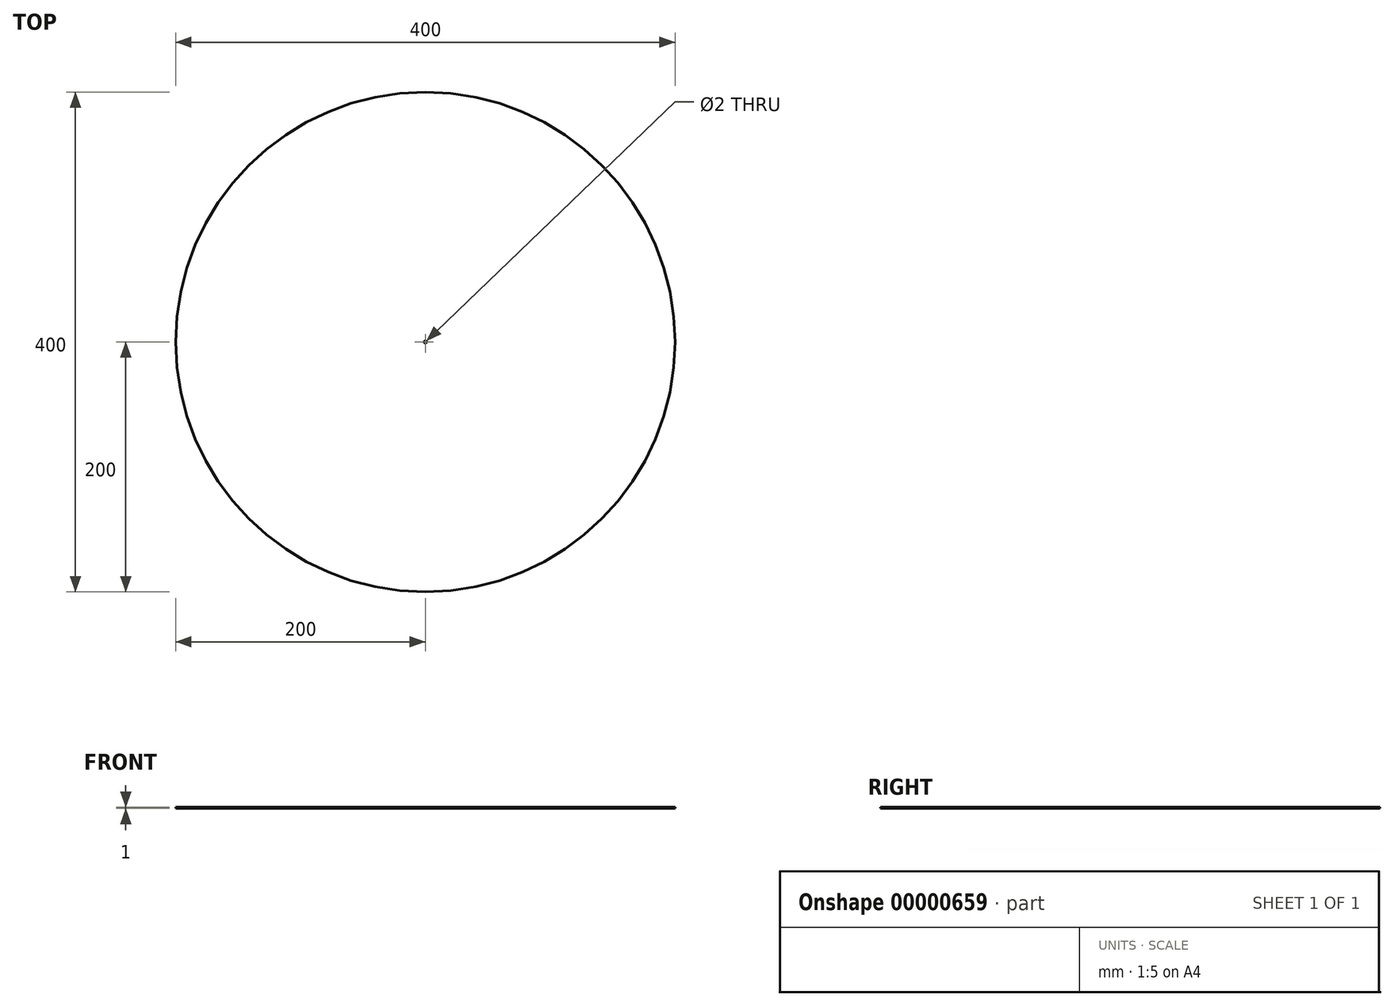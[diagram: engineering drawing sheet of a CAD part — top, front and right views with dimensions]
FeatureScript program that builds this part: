
annotation { "Feature Type Name" : "Feature", "Feature Type Description" : "" }
export const myFeature = defineFeature(function(context is Context, id is Id, definition is map)
    precondition{}
    {
        {
            var Q0;
            Q0=qCreatedBy(makeId("Top.planeOp"),FACE);
            var sketch = newSketch(context, id + "F0", { "sketchPlane" : qUnion([Q0])});
            skCircle(sketch, "E0", {"center": v(0, 0) * mm, "radius": 200 * mm});
            skSolve(sketch);
        }
        {
            var Q0;
            Q0=makeQuery(id+"F0.imprint","IMPRINT",FACE,{"disambiguationData":[TD([[makeQuery(id+"F0.imprint","IMPRINT",EDGE,{"derivedFrom":sQuery(id+"F0.wireOp",EDGE,"E0")}),1.0]])]});
            extrude(context, id + "F1", {"entities" : qUnion([Q0]), "depth" : 1 * mm});
        }
        {
            var Q0;
            Q0=makeQuery(id+"F1.opExtrude","CAP_FACE",FACE,{"disambiguationData":[OSD([sQuery(id+"F0.wireOp",EDGE,"E0")])],"isStart":false});
            var sketch = newSketch(context, id + "F2", { "sketchPlane" : qUnion([Q0])});
            skCircle(sketch, "E1", {"center": v(0, 0) * mm, "radius": 1 * mm});
            skSolve(sketch);
        }
        {
            var Q0;
            Q0=makeQuery(id+"F2.imprint","IMPRINT",FACE,{"disambiguationData":[TD([[makeQuery(id+"F2.imprint","IMPRINT",EDGE,{"derivedFrom":sQuery(id+"F2.wireOp",EDGE,"E1")}),1.0]])]});
            extrude(context, id + "F3", {"entities" : qUnion([Q0]), "operationType" : NewBodyOperationType.REMOVE, "oppositeDirection" : true, "depth" : 14.32 * mm});
        }
    });
